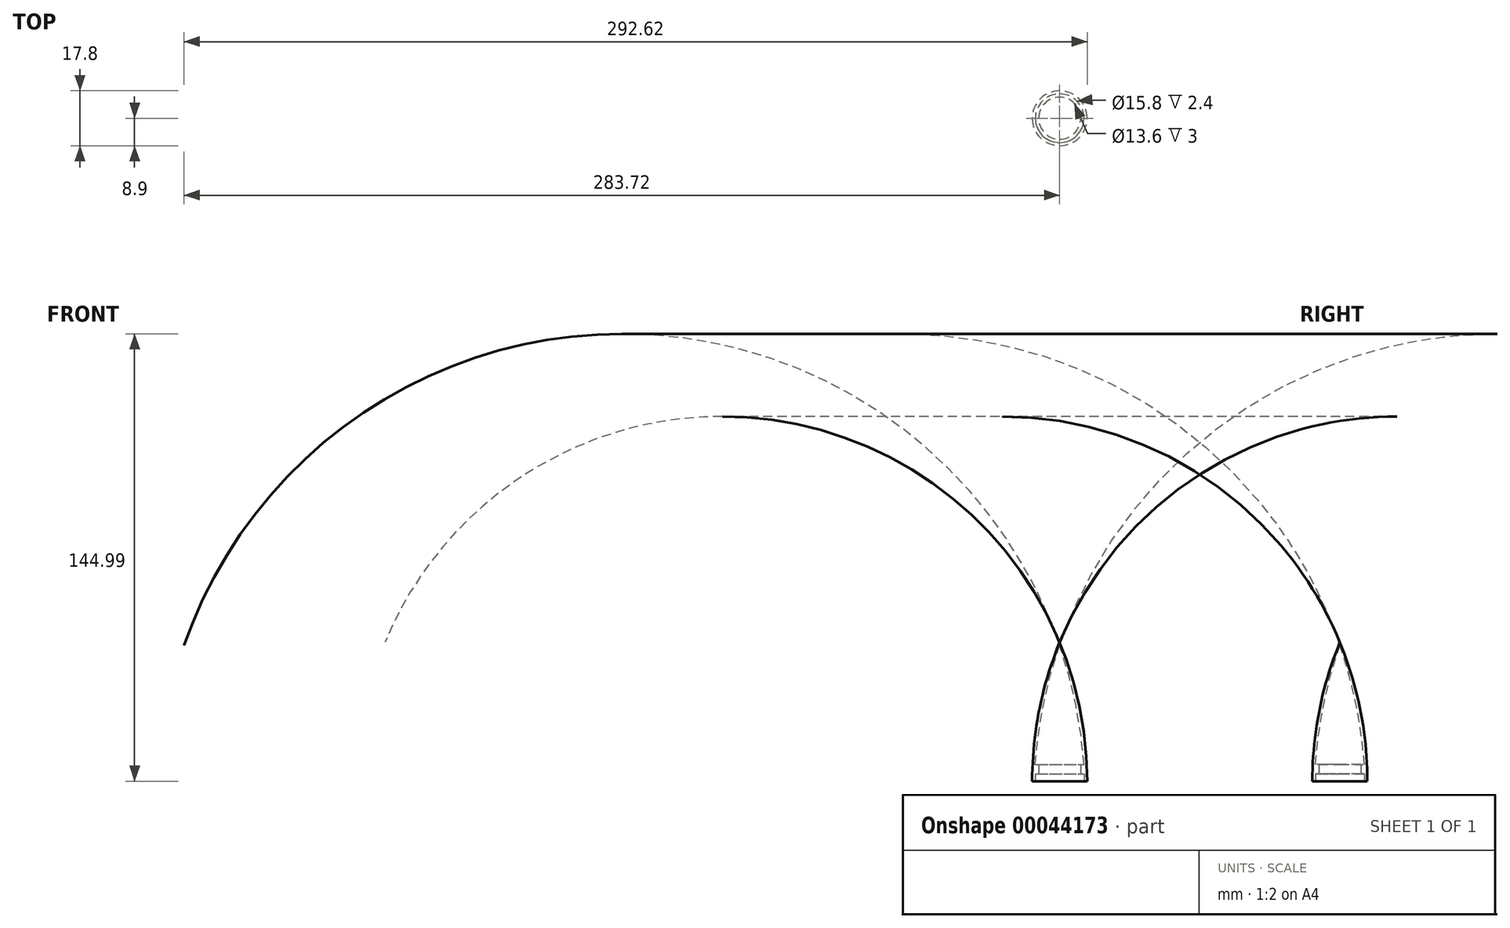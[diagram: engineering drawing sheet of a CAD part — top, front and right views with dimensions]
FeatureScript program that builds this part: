
annotation { "Feature Type Name" : "Feature", "Feature Type Description" : "" }
export const myFeature = defineFeature(function(context is Context, id is Id, definition is map)
    precondition{}
    {
        {
            var Q0;
            Q0=qCreatedBy(makeId("Top.planeOp"),FACE);
            var sketch = newSketch(context, id + "F0", { "sketchPlane" : qUnion([Q0])});
            skLineSegment(sketch, "E0", {"start": v(-17.52, 0) * mm, "end": v(42.68, 0) * mm, "construction": true});
            skLineSegment(sketch, "E1", {"start": v(0, 0) * mm, "end": v(0, 7.9) * mm, "construction": true});
            skLineSegment(sketch, "E2", {"start": v(0, 7.9) * mm, "end": v(2.4, 7.9) * mm});
            skLineSegment(sketch, "E3", {"start": v(2.4, 6.8) * mm, "end": v(2.4, 7.9) * mm});
            skLineSegment(sketch, "E4", {"start": v(2.4, 6.8) * mm, "end": v(5.4, 6.8) * mm});
            skLineSegment(sketch, "E5", {"start": v(0, 7.9) * mm, "end": v(0, 8.9) * mm});
            skArc(sketch, "E6", {"start": v(45, 0) * mm, "mid": v(22.94, 6.65) * mm, "end": v(0, 8.9) * mm});
            skArc(sketch, "E7", {"start": v(44, 0) * mm, "mid": v(24.96, 5.22) * mm, "end": v(5.4, 7.9) * mm});
            skLineSegment(sketch, "E8", {"start": v(44, 0) * mm, "end": v(45, 0) * mm});
            skLineSegment(sketch, "E9", {"start": v(5.4, 6.8) * mm, "end": v(5.4, 7.9) * mm});
            skSolve(sketch);
        }
        {
            var Q0;
            Q0=makeQuery(id+"F0.imprint","IMPRINT",FACE,{"disambiguationData":[TD([[makeQuery(id+"F0.imprint","IMPRINT",EDGE,{"derivedFrom":sQuery(id+"F0.wireOp",EDGE,"E2")}),1.0]])]});
            var Q1;
            Q1=sQuery(id+"F0.wireOp",EDGE,"E0");
            revolve(context, id + "F1", {"entities" : qUnion([Q0]), "axis" : qUnion([Q1]), "revolveType" : RevolveType.FULL});
        }
        {
            var Q0;
            Q0=qCreatedBy(makeId("Front.planeOp"),FACE);
            var sketch = newSketch(context, id + "F2", { "sketchPlane" : qUnion([Q0])});
            skCircle(sketch, "E10", {"center": v(0, 0) * mm, "radius": 8.24 * mm});
            skSolve(sketch);
        }
        {
            var Q0;
            Q0=makeQuery(id+"F1.opRevolve","SWEPT_BODY",BODY,{"disambiguationData":[OSD([sQuery(id+"F0.wireOp",EDGE,"E2"),sQuery(id+"F0.wireOp",EDGE,"E3"),sQuery(id+"F0.wireOp",EDGE,"E4"),sQuery(id+"F0.wireOp",EDGE,"E5"),sQuery(id+"F0.wireOp",EDGE,"E6"),sQuery(id+"F0.wireOp",EDGE,"E7"),sQuery(id+"F0.wireOp",EDGE,"E8"),sQuery(id+"F0.wireOp",EDGE,"E9")])]});
            var Q1;
            Q1=sQuery(id+"F2.wireOp",EDGE,"E10");
            transform(context, id + "F3", {"entities" : qUnion([Q0]), "transformType" : TransformType.ROTATION, "transformAxis" : qUnion([Q1]), "angle" : 90 * degree, "makeCopy" : false});
        }
    });
